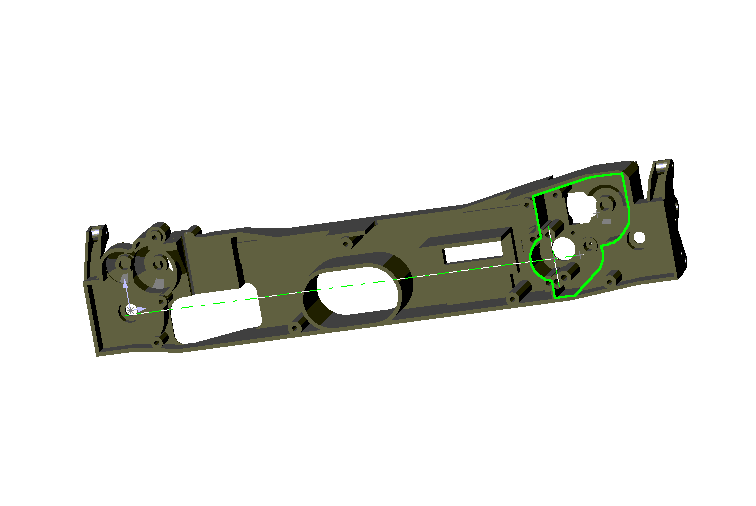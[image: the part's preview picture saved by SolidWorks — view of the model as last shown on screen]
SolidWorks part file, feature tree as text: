
SOLIDWORKS PART (.sldprt)
format: sldprt  version: not decoded by parser v0  size: 2,011,136 bytes
history: native  units: mm
features: sketch x100, extrude x51, cut_extrude x47, fillet x11, chamfer x6, plane x5, cut_revolve x2, material x1 (+8 scaffold rows collapsed)
feature tree (231):
  scaffold x8  (default folders/planes/origin — collapsed)
  material  "Matériau <non spécifié>"
  plane  "Plane1"
  plane  "Plane2"
  plane  "Plane3"
  sketch  "Esquisse1"  dims[c1.D6=40.0mm c1.D9=6.0mm c1.D4=~4.910474mm c1.D11=28.0mm c1.D13=6.0mm c1.D3=10.0mm c1.D18=10.0mm c1.D19=14.0mm c2.D11=28.0mm c2.D15=14.0mm c3.D11=30.0mm c3.D15=1.0mm c4.D11=22.0mm c4.D21=2.0mm c4.D9=2.0mm c4.D10=3.0mm c5.D9=6.0mm c5.D2=18.0mm c5.D5=6.0mm c5.D6=24.0mm c5.D4=12.0mm c5.D1=20.0mm c6.D2=38.0mm c6.D3=35.0mm c6.D4=18.0mm c6.D5=18.0mm c6.D7=12.0mm c6.D8=17.0mm c7.D4=23.0mm c7.D6=21.0mm c8.D4=6.0mm c8.D7=14.0mm c8.D8=25.0mm c8.D10=15.0mm c8.D12=16.0mm c8.D14=22.0mm c8.D15=15.0mm c8.D16=23.0mm c8.D17=8.0mm c8.D19=5.0mm c8.D20=30.0mm c8.D21=23.0mm c9.D14=18.0mm c9.D20=23.0mm c9.D21=16.0mm c9.D10=16.0mm c9.D22=14.0mm c9.D1=23.0mm c9.D2=25.0mm c9.D3=15.0mm c9.D4=~1.474586mm c9.D5=20.0mm c9.D6=5.0mm c9.D7=14.0mm c9.D8=16.0mm c10.D5=20.5mm c10.D9=~21.260292mm c10.D8=2.0mm c11.D9=2.0mm c11.D10=2.0mm c11.D11=0.5mm c11.D1=2.0mm c11.D2=15.2mm c11.D3=23.2mm c11.D5=~34.247688mm c11.D6=19.25mm]
  extrude  "Base-Extrusion"  Depth=11mm
  fillet  "Congé3"  Radius=1mm
  sketch  "Esquisse2"  dims[c1.D6=40.0mm c1.D9=6.0mm c1.D4=~4.910474mm c1.D11=28.0mm c1.D13=6.0mm c1.D3=10.0mm c1.D18=10.0mm c1.D19=14.0mm c2.D11=28.0mm c2.D15=14.0mm c3.D11=30.0mm c3.D15=1.0mm c4.D11=22.0mm c4.D21=2.0mm c4.D9=2.0mm c4.D10=3.0mm c5.D9=6.0mm c5.D2=18.0mm c5.D5=6.0mm c5.D6=24.0mm c5.D1=20.0mm c6.D2=38.0mm c6.D3=35.0mm c6.D4=18.0mm c6.D5=18.0mm c6.D7=12.0mm c6.D8=17.0mm c7.D4=23.0mm c7.D6=21.0mm c8.D4=6.0mm c8.D7=14.0mm c8.D8=25.0mm c8.D10=15.0mm c8.D12=16.0mm c8.D14=22.0mm c8.D15=15.0mm c8.D16=23.0mm c8.D17=8.0mm c8.D19=5.0mm c8.D20=30.0mm c8.D21=23.0mm c9.D14=18.0mm c9.D20=23.0mm c9.D21=16.0mm c9.D10=16.0mm c9.D22=14.0mm c9.D1=23.0mm c9.D2=25.0mm c9.D3=15.0mm c9.D4=~1.474586mm c9.D5=20.0mm c9.D6=5.0mm c9.D7=14.0mm c9.D8=16.0mm c10.D5=20.5mm c10.D9=~21.260292mm c10.D8=2.0mm c11.D9=2.0mm c11.D10=2.0mm c11.D11=0.5mm c11.D1=2.0mm]
  extrude  "Boss.-Extru.1"  Depth=2mm
  sketch  "Esquisse3"
  extrude  "Boss.-Extru.2"  Depth=5mm
  chamfer  "Chanfrein1"  Distance=4mm Angle=45deg
  sketch  "Esquisse6"  dims[D1=28.0mm]
  extrude  "Boss.-Extru.3"  Depth=13mm
  chamfer  "Chanfrein2"  Distance=4mm Angle=45deg
  sketch  "Esquisse8"  dims[D1=10.1mm]
  extrude  "Boss.-Extru.4"  Depth=19mm
  sketch  "Esquisse9"
  cut_extrude  "Enlèv. mat.-Extru.3"  Depth=1mm
  sketch  "Esquisse10"
  cut_extrude  "Enlèv. mat.-Extru.4"  Depth=4mm
  sketch  "Esquisse11"
  sketch  "Esquisse13"  dims[D1=13.0mm]
  extrude  "Boss.-Extru.5"  Depth=4mm
  fillet  "Congé4"  Radius=1mm
  sketch  "Esquisse14"  dims[D1=11.0mm]
  cut_extrude  "Enlèv. mat.-Extru.7"  Depth=4mm
  sketch  "Esquisse15"  dims[D1=6.0mm]
  cut_extrude  "Enlèv. mat.-Extru.8"  [1 undecoded]
  sketch  "Esquisse16"  dims[D1=8.5mm]
  cut_extrude  "Enlèv. mat.-Extru.9"  Depth=0.5mm
  sketch  "Esquisse17"  dims[D1=5.0mm D2=9.0mm]
  extrude  "Boss.-Extru.6"  Depth=4mm
  plane  "Plan1"  Offset=11mm
  sketch  "Esquisse20"  dims[c1.D8=7.0mm c1.D1=18.0mm c1.D2=12.0mm c2.D1=8.0mm c2.D2=4.0mm c2.D3=14.0mm c2.D4=130.0mm c2.D5=22.0mm c2.D6=174.5mm c2.D7=22.0mm]
  extrude  "Boss.-Extru.9"  Depth=33mm
  sketch  "Esquisse21"  dims[c1.D1=18.0mm c1.D2=12.0mm c2.D1=8.0mm c2.D2=4.0mm c2.D3=14.0mm c2.D4=130.0mm c2.D5=22.0mm c2.D6=175.0mm]
  cut_extrude  "Enlèv. mat.-Extru.10"  [1 undecoded]
  chamfer  "Chanfrein3"  Distance=21mm
  plane  "Plan2"  Offset=17mm
  sketch  "Esquisse22"  dims[c1.D1=7.0mm c1.D6=7.0mm c1.D7=3.5mm c1.D2=~3.437668mm c1.D8=3.5mm c2.D2=11.0mm c2.D3=15.0mm c2.D4=~7.335312mm c3.D4=45.0deg c3.D5=3.0mm c3.D6=7.5mm c3.D1=8.0mm c4.D6=3.0mm c4.D1=6.0mm c4.D2=8.0mm c4.D4=20.0mm c5.D1=4.0mm c5.D2=6.0mm c5.D3=11.0mm c5.D4=~20.022765mm c5.D5=24.5mm c5.D6=20.0mm c5.D7=39.0mm c6.D2=~17.486229mm c6.D3=11.0mm c6.D5=18.0mm c7.D2=11.0mm c7.D3=6.0mm c7.D4=15.0mm c7.D5=18.0mm c7.D9=2.0mm c7.D10=~12.040627mm]
  extrude  "Boss.-Extru.10"  Depth=18mm
  cut_extrude  "Enlèv. mat.-Extru.11"  Depth=10mm
  sketch  "Esquisse23"  dims[D1=24.0mm]
  cut_extrude  "Enlèv. mat.-Extru.12"  Depth=4mm
  sketch  "Esquisse24"  dims[c1.D1=6.0mm c1.D2=3.0mm c2.D1=5.0mm c2.D2=9.0mm]
  extrude  "Boss.-Extru.12"  Depth=4mm
  sketch  "Esquisse25"  dims[D1=4.0mm D2=10.0mm D3=3.0mm D4=2.0mm D5=6.0mm D6=5.5mm D7=11.5mm D8=5.5mm]
  cut_revolve  "Enlèvement de matière-Révolution1"  Angle=360deg
  sketch  "Esquisse27"  dims[D1=12.0mm]
  extrude  "Boss.-Extru.13"  Depth=4mm
  sketch  "Esquisse28"
  extrude  "Boss.-Extru.14"  Depth=14mm
  sketch  "Esquisse29"  dims[D1=45.0mm D2=12.0mm D3=22.0mm D4=18.0mm D5=15.0mm D6=40.0mm D7=20.0mm D8=35.0mm]
  extrude  "Boss.-Extru.15"  Depth=22mm
  sketch  "Esquisse30"  dims[c1.D2=36.0mm c1.D1=34.0mm c1.D5=24.0mm c1.D6=17.0mm c1.D7=12.0mm c1.D10=16.5mm c1.D11=~11.949177mm c2.D1=222.0mm c2.D3=27.0mm c3.D1=217.0mm c3.D3=228.0mm c4.D1=22.8mm c4.D4=19.0mm c5.D1=22.8mm c5.D4=13.0mm c5.D5=14.0mm c5.D6=18.0mm c5.D8=30.0mm c5.D9=2.0mm c5.D2=2.0mm c6.D9=~17.995555mm c6.D6=~17.995555mm c6.D5=19.25mm c7.D6=18.0mm c7.D9=21.0mm]
  cut_extrude  "Enlèv. mat.-Extru.13"  Depth=20mm
  fillet  "Congé5"  Radius=3mm
  fillet  "Congé6"  Radius=6mm
  sketch  "Esquisse33"  dims[D1=9.0mm D2=5.0mm]
  extrude  "Boss.-Extru.16"  Depth=1mm
  sketch  "Esquisse35"  dims[c1.D1=2.0mm c1.D2=~35.146836mm c2.D2=180.0deg c3.D2=~39.661277mm c4.D2=180.0deg c4.D3=~4.241514mm c4.D4=40.0mm c5.D2=2.0mm c5.D1=2.0mm c6.D2=61.0mm]
  cut_extrude  "Enlèv. mat.-Extru.16"  Depth=10mm
  sketch  "Esquisse39"  dims[c1.D1=15.0mm c1.D2=21.0mm c2.D1=35.0mm c2.D2=~19.265546mm]
  cut_extrude  "Enlèv. mat.-Extru.17"  Depth=11mm
  sketch  "Esquisse40"  dims[D1=20.0mm]
  extrude  "Boss.-Extru.17"  Depth=2mm
  sketch  "Esquisse41"  dims[D1=20.0mm]
  cut_extrude  "Enlèv. mat.-Extru.18"  Depth=2mm
  sketch  "Esquisse42"  dims[c1.D1=9.0mm c1.D2=5.0mm c2.D1=9.0mm c2.D2=5.0mm]
  extrude  "Boss.-Extru.18"  Depth=5mm
  sketch  "Esquisse43"  dims[D1=22.8mm D2=13.0mm]
  extrude  "Boss.-Extru.19"  Depth=5mm
  fillet  "Congé7"  Radius=1mm
  sketch  "Esquisse44"  dims[D1=5.0mm]
  cut_extrude  "Enlèv. mat.-Extru.19"  Depth=5mm
  sketch  "Esquisse45"  dims[c1.D2=11.0mm c1.D1=23.2mm c2.D2=23.2mm c2.D3=~25.166952mm c2.D1=11.0mm c3.D2=23.2mm c3.D3=27.5mm c3.D4=~14.499445mm]
  sketch  "Esquisse48"  dims[D1=15.0mm D2=27.5mm D3=23.2mm]
  extrude  "Boss.-Extru.21"  Depth=4mm
  cut_extrude  "Enlèv. mat.-Extru.20"  Depth=4mm
  sketch  "Esquisse49"  dims[D1=6.0mm]
  cut_extrude  "Enlèv. mat.-Extru.21"  [1 undecoded]
  sketch  "Esquisse50"  dims[D1=33.0mm]
  cut_extrude  "Enlèv. mat.-Extru.22"  Depth=4mm
  sketch  "Esquisse51"  dims[D1=11.5mm]
  cut_extrude  "Enlèv. mat.-Extru.23"  Depth=14mm
  sketch  "Esquisse52"  dims[D1=12.0mm]
  cut_extrude  "Enlèv. mat.-Extru.24"  [1 undecoded]
  sketch  "Esquisse53"  dims[D2=8.0mm D1=34.0mm]
  extrude  "Boss.-Extru.22"  Depth=10mm
  chamfer  "Chanfrein7"  Distance=5mm Angle=45deg
  sketch  "Esquisse54"  dims[c1.D1=5.0mm c1.D2=~135.966117mm c2.D1=5.0mm c2.D2=~25.60601mm c2.D3=~18.651473mm c3.D1=~25.60601mm c3.D2=~91.708634mm c3.D3=17.5mm c4.D2=~134.814644mm c4.D3=~18.078005mm c4.D1=135.0mm c5.D2=25.5mm c5.D3=18.0mm c5.D4=5.0mm]
  sketch  "Esquisse56"  dims[c1.D1=7.0mm c1.D6=7.0mm c1.D7=3.5mm c1.D17=~3.491006mm c1.D18=~3.437668mm c2.D1=3.5mm c2.D2=11.0mm c2.D3=15.0mm c2.D4=~7.335312mm c3.D4=45.0deg c3.D5=3.0mm c3.D6=7.5mm c3.D1=8.0mm c4.D6=3.0mm c4.D1=6.0mm c4.D2=8.0mm c4.D4=20.0mm c5.D1=15.0mm c5.D2=7.5mm c5.D3=42.0mm c5.D4=~16.327469mm c5.D5=~8.115097mm c5.D6=6.0mm c5.D7=~6.246428mm c5.D8=6.0mm c5.D9=~6.246428mm c5.D10=8.0mm c5.D11=18.0mm c5.D12=3.0mm c6.D12=~174.959701deg c7.D12=3.0mm c7.D13=3.0mm c7.D14=9.0mm c7.D15=~19.818475mm c7.D16=3.0mm c7.D19=24.0mm c7.D20=12.0mm c7.D21=~40.680021mm c7.D22=4.0mm c7.D23=16.33mm c7.D24=~40.319979mm c7.D3=39.0mm c8.D24=18.0mm c8.D1=~8.580635mm c8.D2=4.0mm c8.D3=39.0mm c8.D4=4.0mm c8.D5=6.0mm c8.D6=11.0mm c8.D7=~7.500014mm c8.D8=~8.995515mm c9.D2=~6.246421mm c9.D7=~4.750901mm c9.D8=~4.495512mm c9.D9=15.0mm c9.D10=28.0mm c9.D3=~1.996637mm c10.D10=7.0mm c10.D11=~4.640503mm]
  extrude  "Boss.-Extru.23"  Depth=6mm
  sketch  "Esquisse58"  dims[c1.D1=11.5mm c1.D2=2.0mm c1.D3=4.0mm c1.D4=6.0mm c1.D5=10.0mm c1.D6=3.0mm c1.D7=11.5mm c1.D8=11.5mm c2.D1=~6.254445mm c2.D2=5.75mm c2.D3=5.5mm c2.D7=2.0mm c2.D8=4.0mm c2.D9=~4.995555mm c3.D1=5.5mm]
  cut_revolve  "Enlèvement de matière-Révolution2"  Angle=360deg
  sketch  "Esquisse59"
  extrude  "Boss.-Extru.24"  [1 undecoded]
  sketch  "Esquisse60"  dims[D1=5.0mm]
  cut_extrude  "Enlèv. mat.-Extru.27"  Depth=5mm
  sketch  "Esquisse61"  dims[D1=7.0mm D2=3.0mm D3=4.0mm]
  extrude  "Boss.-Extru.25"  Depth=9mm
  sketch  "Esquisse62"  dims[D1=3.0mm]
  cut_extrude  "Enlèv. mat.-Extru.28"  Depth=9mm
  sketch  "Esquisse63"  dims[D1=7.0mm D2=4.0mm]
  extrude  "Boss.-Extru.26"  Depth=9mm
  sketch  "Esquisse64"  dims[D1=3.0mm]
  cut_extrude  "Enlèv. mat.-Extru.29"  Depth=9mm
  sketch  "Esquisse65"
  cut_extrude  "Enlèv. mat.-Extru.31"  Depth=9mm
  sketch  "Esquisse66"  dims[D1=1.5mm]
  cut_extrude  "Enlèv. mat.-Extru.32"  [1 undecoded]
  chamfer  "Chanfrein11"  Distance=5mm
  cut_extrude  "Enlèv. mat.-Extru.33"  [1 undecoded]
  sketch  "Esquisse68"  dims[D1=9.0mm]
  cut_extrude  "Enlèv. mat.-Extru.34"  Depth=7mm
  sketch  "Esquisse70"  dims[c1.D4=5.0mm c1.D8=3.0mm c1.D15=3.0mm c1.D1=13.0mm c1.D2=32.0mm c1.D3=75.0mm c1.D5=20.0mm c1.D6=72.0mm c1.D7=22.0mm c1.D9=13.0mm c1.D10=75.0mm c1.D11=20.0mm c1.D12=32.0mm c1.D13=13.0mm c1.D14=22.0mm c2.D15=22.0mm c2.D13=72.0mm c2.D1=40.0mm]
  sketch  "Esquisse71"
  cut_extrude  "Enlèv. mat.-Extru.36"  Depth=10mm
  sketch  "Esquisse73"
  cut_extrude  "Enlèv. mat.-Extru.37"  Depth=10mm
  chamfer  "Chanfrein12"  Distance=14mm
  sketch  "Esquisse74"  dims[D1=90.0mm D2=90.0mm D3=2.0mm D4=~43.147963mm]
  cut_extrude  "Enlèv. mat.-Extru.38"  Depth=5mm
  sketch  "Esquisse75"  dims[D1=172.0mm D2=41.0mm]
  cut_extrude  "Enlèv. mat.-Extru.39"  Depth=3mm
  sketch  "Esquisse76"  dims[c1.D1=3.0mm c1.D2=3.0mm c2.D1=5.0mm c2.D3=3.0mm c2.D2=3.0mm c2.D5=3.0mm c2.D6=5.0mm c2.D4=8.0mm c3.D5=5.0mm c3.D3=6.0mm c3.D4=32.0mm c3.D2=~41.196606mm c4.D3=41.2mm]
  cut_extrude  "Enlèv. mat.-Extru.40"  [1 undecoded]
  cut_extrude  "Enlèv. mat.-Extru.41"  Depth=65mm
  sketch  "Esquisse77"  dims[D1=14.0mm D2=20.0mm D4=122.0mm D3=2.0mm]
  extrude  "Boss.-Extru.27"  [1 undecoded]
  sketch  "Esquisse78"  dims[c1.D1=14.0mm c1.D2=20.0mm c2.D1=122.0mm c2.D3=2.0mm]
  cut_extrude  "Enlèv. mat.-Extru.42"  [1 undecoded]
  sketch  "Esquisse79"  dims[D1=10.0mm]
  extrude  "Boss.-Extru.28"  Depth=2mm
  fillet  "Congé8"  Radius=1mm
  sketch  "Esquisse81"  dims[c1.D3=7.0mm c1.D6=9.0mm c1.D9=7.0mm c2.D3=7.0mm c2.D1=21.0mm c2.D2=5.0mm c2.D4=27.0mm c2.D5=23.0mm c2.D7=19.0mm c2.D8=29.0mm c2.D9=29.0mm c2.D10=23.0mm c2.D11=18.0mm c3.D4=~15.138462mm]
  extrude  "Boss.-Extru.30"  Depth=1.5mm
  sketch  "Esquisse82"  dims[D1=7.0mm]
  extrude  "Boss.-Extru.31"  Depth=22.5mm
  sketch  "Esquisse83"  dims[D1=8.0mm]
  extrude  "Boss.-Extru.32"  Depth=4mm
  sketch  "Esquisse85"
  extrude  "Boss.-Extru.34"  Depth=6mm
  sketch  "Esquisse86"
  extrude  "Boss.-Extru.35"  Depth=1.5mm
  sketch  "Esquisse87"  dims[D1=3.0mm D2=4.0mm D3=2.0mm]
  cut_extrude  "Enlèv. mat.-Extru.43"  [1 undecoded]
  sketch  "Esquisse90"  dims[c1.D1=2.0mm c1.D2=2.0mm c1.D3=2.0mm c1.D4=2.0mm c2.D1=~4.995667mm]
  cut_extrude  "Enlèv. mat.-Extru.45"  Depth=10mm
  sketch  "Esquisse91"  dims[D1=9.0mm D2=6.0mm D3=6.0mm]
  extrude  "Boss.-Extru.36"  Depth=7mm
  fillet  "Congé9"  Radius=1mm
  sketch  "Esquisse92"  dims[D1=8.5mm]
  cut_extrude  "Enlèv. mat.-Extru.46"  Depth=0.5mm
  sketch  "Esquisse93"  dims[D5=8.0mm D6=2.0mm D1=27.0mm D2=23.0mm D3=24.0mm D4=32.0mm D7=21.0mm]
  extrude  "Boss.-Extru.37"  Depth=1.5mm
  sketch  "Esquisse95"
  extrude  "Boss.-Extru.42"  Depth=22.5mm
  sketch  "Esquisse96"  dims[D1=8.0mm]
  extrude  "Boss.-Extru.43"  Depth=4mm
  sketch  "Esquisse98"
  extrude  "Boss.-Extru.44"  Depth=6.5mm
  sketch  "Esquisse99"
  extrude  "Boss.-Extru.47"  Depth=1.5mm
  sketch  "Esquisse100"  dims[D1=3.0mm D2=4.0mm D3=4.0mm]
  cut_extrude  "Enlèv. mat.-Extru.47"  [1 undecoded]
  sketch  "Esquisse101"  dims[c1.D4=2.0mm c1.D5=2.0mm c1.D1=10.0mm c1.D2=17.0mm c1.D3=15.6mm c2.D5=~94.931251mm]
  cut_extrude  "Enlèv. mat.-Extru.48"  Depth=10mm
  sketch  "Esquisse102"  dims[D4=2.0mm D5=2.0mm D1=10.0mm D2=17.0mm D3=15.6mm]
  cut_extrude  "Enlèv. mat.-Extru.49"  Depth=10mm
  fillet  "Congé10"  Radius=1mm
  sketch  "Esquisse103"  dims[c1.D1=3.0mm c1.D5=3.0mm c1.D2=~15.613009mm c1.D3=~15.629288mm c1.D4=25.0mm c1.D6=~1.766385mm c1.D7=~2.185356mm c1.D8=~0.964331mm c1.D9=~0.964331mm c1.D10=~0.964331mm c1.D11=~1.766385mm c1.D12=~2.185356mm c1.D13=10.0mm c1.D14=10.0mm c1.D15=~15.613009mm c2.D2=~14.035669mm c2.D15=14.0mm c2.D16=3.75mm c2.D17=3.75mm c2.D18=20.0mm]
  extrude  "Boss.-Extru.48"  Depth=32mm
  sketch  "Esquisse104"
  extrude  "Boss.-Extru.49"  Depth=1mm
  fillet  "Congé11"  Radius=1mm
  sketch  "Esquisse105"  dims[D1=4.0mm D2=5.0mm D3=11.0mm]
  extrude  "Boss.-Extru.50"  Depth=8mm
  fillet  "Congé12"  Radius=2mm
  sketch  "Esquisse106"  dims[D2=2.0mm D1=10.0mm D3=6.0mm]
  cut_extrude  "Enlèv. mat.-Extru.50"  Depth=18mm
  sketch  "Esquisse107"  dims[D1=42.0mm D2=23.0mm D3=21.0mm]
  extrude  "Boss.-Extru.51"  Depth=5mm
  sketch  "Esquisse108"  dims[D1=2.0mm]
  extrude  "Boss.-Extru.52"  Depth=20mm
  sketch  "Esquisse109"  dims[D1=12.0mm D2=90.0mm D3=30.0mm]
  cut_extrude  "Enlèv. mat.-Extru.51"  [1 undecoded]
  sketch  "Esquisse111"
  cut_extrude  "Enlèv. mat.-Extru.54"  Depth=5mm
  sketch  "Esquisse114"  dims[D2=7.0mm D1=5.0mm D3=10.0mm]
  extrude  "Boss.-Extru.53"  Depth=26mm
  sketch  "Esquisse115"  dims[D4=7.0mm D5=7.0mm D6=7.0mm D1=5.0mm D2=78.0mm D3=33.0mm D7=93.75mm D8=7.25mm]
  extrude  "Boss.-Extru.54"  [1 undecoded]
  sketch  "Esquisse119"  dims[D1=6.0mm D2=6.0mm D3=3.0mm D4=3.0mm]
  extrude  "Boss.-Extru.56"  Depth=3mm
  sketch  "Esquisse120"  dims[D1=2.5mm]
  cut_extrude  "Enlèv. mat.-Extru.58"  Depth=15mm
  sketch  "Esquisse121"  dims[c1.D1=6.0mm c1.D2=6.0mm c1.D3=3.0mm c1.D4=~2.310108mm c2.D1=6.0mm c2.D2=6.0mm c2.D3=3.0mm c2.D4=3.0mm]
  extrude  "Boss.-Extru.57"  Depth=3mm
  sketch  "Esquisse122"  dims[D1=2.5mm]
  cut_extrude  "Enlèv. mat.-Extru.59"  Depth=10mm
  sketch  "Esquisse123"  dims[c1.D2=25.0mm c1.D6=3.0mm c1.D7=3.0mm c1.D8=3.0mm c1.D9=3.0mm c1.D10=3.0mm c1.D11=3.0mm c1.D12=25.0mm c1.D1=16.0mm c1.D3=~25.847553mm c2.D3=10.0deg c2.D4=~24.781102mm c3.D3=12.5mm c4.D3=10.0deg c4.D4=28.0mm c5.D4=10.0deg c5.D5=12.5mm c6.D5=40.0deg c6.D9=~7.239814mm c6.D11=~0.969743mm c6.D2=12.0mm c6.D3=12.0mm c6.D4=12.0mm c7.D5=12.0mm c7.D11=12.0mm c7.D12=12.0mm]
  sketch  "Esquisse124"  dims[D1=7.0mm D2=7.0mm D3=7.0mm D4=7.0mm D5=7.0mm D6=7.0mm]
  extrude  "Boss.-Extru.58"  Depth=20mm
  cut_extrude  "Enlèv. mat.-Extru.60"  [1 undecoded]
  sketch  "Esquisse125"
  cut_extrude  "Enlèv. mat.-Extru.61"  [1 undecoded]
  sketch  "Esquisse127"  dims[D1=~12.617216mm]
  extrude  "Boss.-Extru.59"  [1 undecoded]
  sketch  "Esquisse128"  dims[c1.D2=7.0mm c1.D3=7.0mm c1.D1=15.0mm c2.D2=3.0mm c2.D4=~4.906028mm]
  extrude  "Boss.-Extru.60"  [1 undecoded]
  sketch  "Esquisse129"  dims[D1=6.0mm D2=6.0mm]
  extrude  "Boss.-Extru.61"  [1 undecoded]
  sketch  "Esquisse130"  dims[D2=7.0mm D1=33.5mm D3=5.0mm]
  extrude  "Boss.-Extru.62"  [1 undecoded]
  sketch  "Esquisse131"  dims[D1=2.5mm D2=2.5mm D3=2.5mm D4=2.5mm D5=2.5mm D6=2.5mm D7=2.5mm D8=2.5mm D9=2.5mm]
  cut_extrude  "Enlèv. mat.-Extru.62"  Depth=10mm
  sketch  "Esquisse132"  dims[D1=8.0mm D2=8.0mm D3=17.0mm D4=4.5mm D5=7.0mm]
  extrude  "Boss.-Extru.63"  Depth=24mm
  sketch  "Esquisse133"  dims[D1=2.0mm D2=2.0mm]
  cut_extrude  "Enlèv. mat.-Extru.63"  Depth=10mm
  fillet  "Congé13"  Radius=0.3mm
decode coverage: 180 of 217 modeling features carry decoded parameters
note: ~ marks probable driven/reference dimensions
note: 20 parameter values undecoded
summary: no parameter record found for 20 features
note: suppression state not decoded; provenance and decode notes live in map.json
